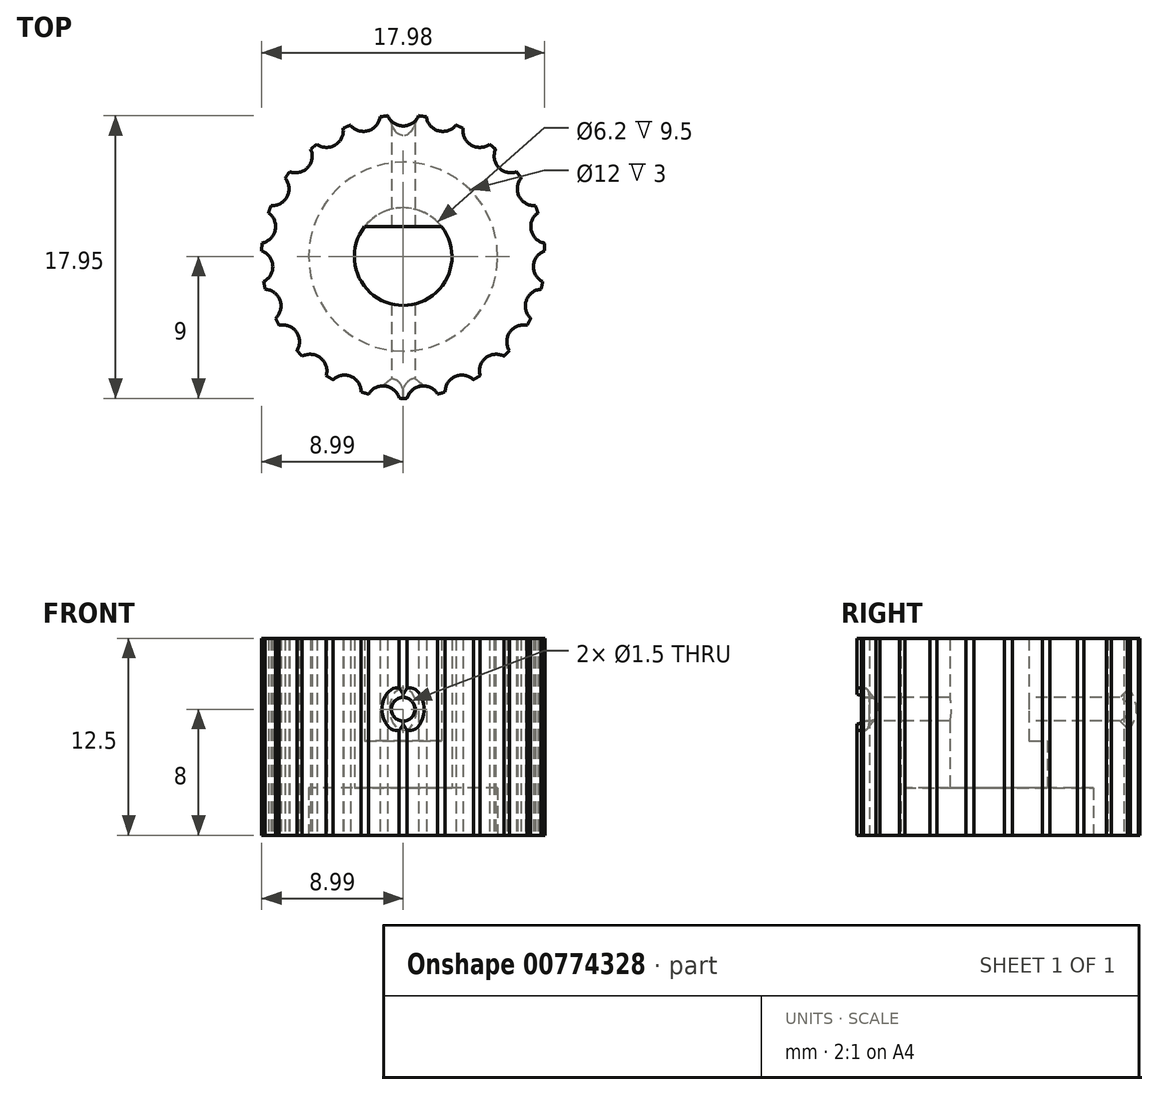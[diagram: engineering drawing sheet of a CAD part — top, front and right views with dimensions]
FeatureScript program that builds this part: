
annotation { "Feature Type Name" : "Feature", "Feature Type Description" : "" }
export const myFeature = defineFeature(function(context is Context, id is Id, definition is map)
    precondition{}
    {
        {
            var Q0;
            Q0=qCreatedBy(makeId("Top.planeOp"),FACE);
            var sketch = newSketch(context, id + "F0", { "sketchPlane" : qUnion([Q0])});
            skPoint(sketch, "E0", {"position": v(0, 0) * mm});
            skCircle(sketch, "E1", {"center": v(0, 0) * mm, "radius": 9 * mm});
            skSolve(sketch);
        }
        {
            var Q0;
            Q0 = qSketchRegion(id + "F0", true);
            extrude(context, id + "F1", {"entities" : qUnion([Q0]), "depth" : 13 * mm, "offsetDistance" : 25 * mm, "hasSecondDirection" : true, "secondDirectionOppositeDirection" : false, "secondDirectionDepth" : 0.5 * mm});
        }
        {
            var Q0;
            Q0=qCreatedBy(makeId("Top.planeOp"),FACE);
            var sketch = newSketch(context, id + "F2", { "sketchPlane" : qUnion([Q0])});
            skLineSegment(sketch, "E2", {"start": v(0, 0) * mm, "end": v(0, 7.73) * mm, "construction": true});
            skLineSegment(sketch, "E3", {"start": v(-1, 9) * mm, "end": v(0, 9) * mm});
            skLineSegment(sketch, "E4", {"start": v(0, 9) * mm, "end": v(1, 9) * mm});
            skArc(sketch, "E5", {"start": v(-1, 9) * mm, "mid": v(0, 8.3) * mm, "end": v(1, 9) * mm});
            skSolve(sketch);
        }
        {
            var Q0;
            Q0=qCreatedBy(makeId("Front.planeOp"),FACE);
            var sketch = newSketch(context, id + "F3", { "sketchPlane" : qUnion([Q0])});
            skLineSegment(sketch, "E6", {"start": v(0, 42) * mm, "end": v(0, 0) * mm, "construction": true});
            skSolve(sketch);
        }
        {
            var Q0;
            Q0 = qSketchRegion(id + "F2", true);
            extrude(context, id + "F4", {"entities" : qUnion([Q0]), "depth" : 25 * mm, "offsetDistance" : 25 * mm});
        }
        {
            var Q0;
            Q0=makeQuery(id+"F4.opExtrude","SWEPT_BODY",BODY,{"disambiguationData":[OSD([sQuery(id+"F2.wireOp",EDGE,"E3"),sQuery(id+"F2.wireOp",EDGE,"E4"),sQuery(id+"F2.wireOp",EDGE,"E5")])]});
            var Q1;
            Q1=sQuery(id+"F3.wireOp",EDGE,"E6");
            circularPattern(context, id + "F5", {"operationType" : NewBodyOperationType.REMOVE, "entities" : qUnion([Q0]), "axis" : qUnion([Q1]), "angle" : 360 * degree, "instanceCount" : 23, "equalSpace" : true, "computeTransformsWithoutBuiltin" : true});
        }
        {
            var Q0;
            Q0=qCreatedBy(makeId("Top.planeOp"),FACE);
            var sketch = newSketch(context, id + "F6", { "sketchPlane" : qUnion([Q0])});
            skCircle(sketch, "E7", {"center": v(0, 0) * mm, "radius": 3.1 * mm});
            skSolve(sketch);
        }
        {
            var Q0;
            Q0 = qSketchRegion(id + "F6", true);
            extrude(context, id + "F7", {"entities" : qUnion([Q0]), "operationType" : NewBodyOperationType.REMOVE, "depth" : 13 * mm, "offsetDistance" : 25 * mm});
        }
        {
            var Q0;
            Q0=qCreatedBy(makeId("Top.planeOp"),FACE);
            var sketch = newSketch(context, id + "F8", { "sketchPlane" : qUnion([Q0])});
            skCircle(sketch, "E8", {"center": v(0, 0) * mm, "radius": 6 * mm});
            skSolve(sketch);
        }
        {
            var Q0;
            Q0 = qSketchRegion(id + "F8", true);
            extrude(context, id + "F9", {"entities" : qUnion([Q0]), "operationType" : NewBodyOperationType.REMOVE, "depth" : 3.5 * mm, "offsetDistance" : 25 * mm});
        }
        {
            var Q0;
            Q0=qCreatedBy(makeId("Top.planeOp"),FACE);
            var sketch = newSketch(context, id + "F10", { "sketchPlane" : qUnion([Q0])});
            skArc(sketch, "E9", {"start": v(2.45, 1.9) * mm, "mid": v(0, 3.1) * mm, "end": v(-2.45, 1.9) * mm});
            skLineSegment(sketch, "E10", {"start": v(-2.45, 1.9) * mm, "end": v(2.45, 1.9) * mm});
            skSolve(sketch);
        }
        {
            var Q0;
            Q0 = qSketchRegion(id + "F10", true);
            extrude(context, id + "F11", {"entities" : qUnion([Q0]), "operationType" : NewBodyOperationType.ADD, "depth" : 13 * mm, "offsetDistance" : 25 * mm, "hasSecondDirection" : true, "secondDirectionOppositeDirection" : false, "secondDirectionDepth" : 6.5 * mm});
        }
        {
            var Q0;
            Q0=qCreatedBy(makeId("Front.planeOp"),FACE);
            var sketch = newSketch(context, id + "F12", { "sketchPlane" : qUnion([Q0])});
            skCircle(sketch, "E11", {"center": v(0, 8.5) * mm, "radius": 0.75 * mm});
            skSolve(sketch);
        }
        {
            var Q0;
            Q0 = qSketchRegion(id + "F12", true);
            extrude(context, id + "F13", {"entities" : qUnion([Q0]), "operationType" : NewBodyOperationType.REMOVE, "endBound" : BoundingType.THROUGH_ALL, "oppositeDirection" : true, "depth" : 25 * mm, "offsetDistance" : 25 * mm, "hasSecondDirection" : true, "secondDirectionBound" : BoundingType.THROUGH_ALL, "secondDirectionOppositeDirection" : false, "secondDirectionDepth" : 25 * mm});
        }
        {
            var Q0;
            Q0=makeQuery(id+"F13.boolean.opBoolean","INTERSECT",EDGE,{"derivedFrom":[makeQuery(id+"F5.boolean.opBoolean","COPY",FACE,{"derivedFrom":makeQuery(id+"F4.opExtrude","SWEPT_FACE",FACE,{"disambiguationData":[OSD([sQuery(id+"F2.wireOp",EDGE,"E5")])]})}),makeQuery(id+"F13.opExtrude","SWEPT_FACE",FACE,{"disambiguationData":[OSD([sQuery(id+"F12.wireOp",EDGE,"E11")])]})]});
            var Q1;
            Q1=makeQuery(id+"F13.boolean.opBoolean","INTERSECT",EDGE,{"derivedFrom":[makeQuery(id+"F5.boolean.opBoolean","COPY",FACE,{"derivedFrom":makeQuery(id+"F5.opPattern","COPY",FACE,{"derivedFrom":makeQuery(id+"F4.opExtrude","SWEPT_FACE",FACE,{"disambiguationData":[OSD([sQuery(id+"F2.wireOp",EDGE,"E5")])]}),"instanceName":"12"})}),makeQuery(id+"F13.opExtrude","SWEPT_FACE",FACE,{"disambiguationData":[OSD([sQuery(id+"F12.wireOp",EDGE,"E11")])]})]});
            var Q2;
            Q2=makeQuery(id+"F13.boolean.opBoolean","INTERSECT",EDGE,{"derivedFrom":[makeQuery(id+"F5.boolean.opBoolean","COPY",FACE,{"derivedFrom":makeQuery(id+"F5.opPattern","COPY",FACE,{"derivedFrom":makeQuery(id+"F4.opExtrude","SWEPT_FACE",FACE,{"disambiguationData":[OSD([sQuery(id+"F2.wireOp",EDGE,"E5")])]}),"instanceName":"11"})}),makeQuery(id+"F13.opExtrude","SWEPT_FACE",FACE,{"disambiguationData":[OSD([sQuery(id+"F12.wireOp",EDGE,"E11")])]})]});
            chamfer(context, id + "F14", {"entities" : qUnion([Q0, Q1, Q2]), "width" : 0.6 * mm, "tangentPropagation" : true});
        }
    });
